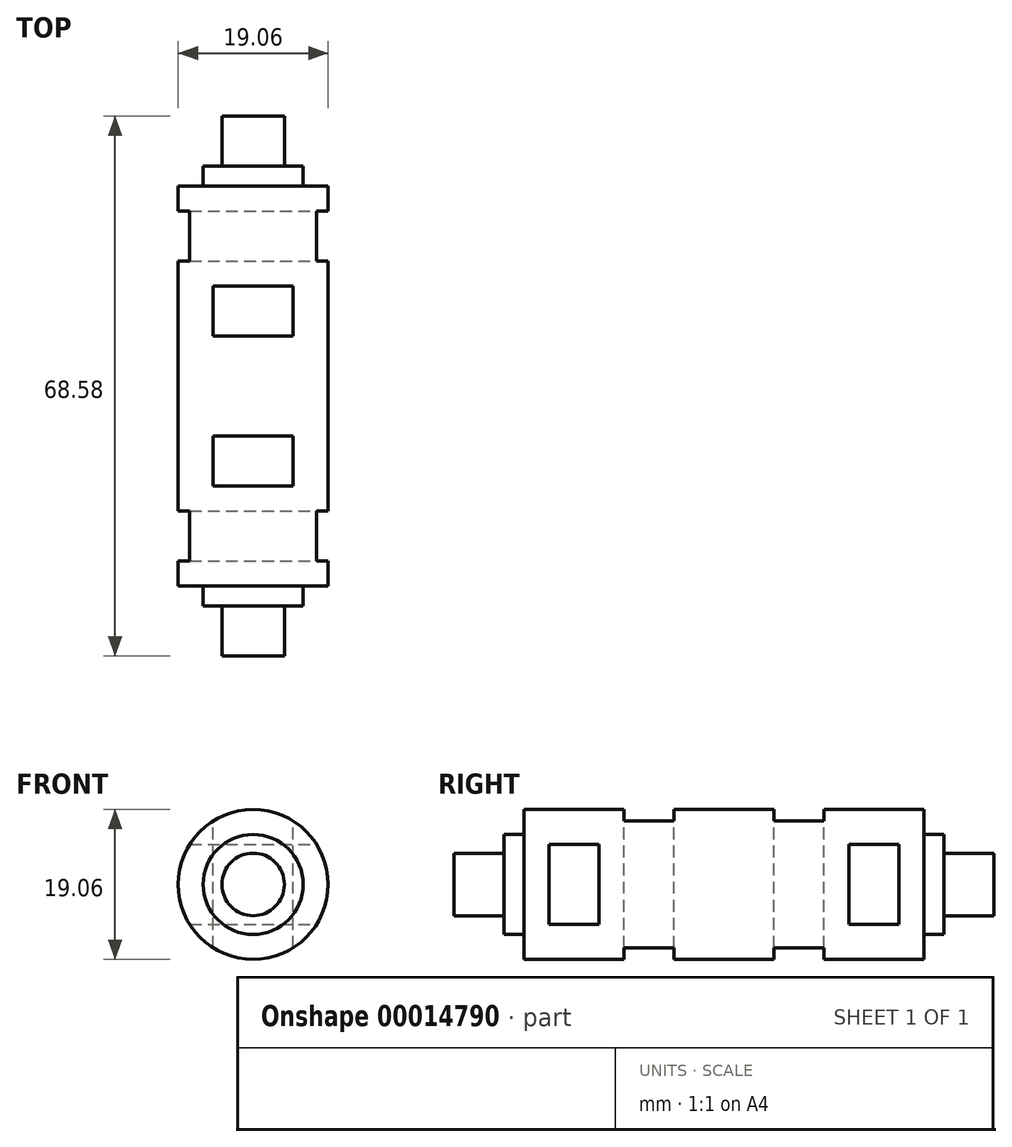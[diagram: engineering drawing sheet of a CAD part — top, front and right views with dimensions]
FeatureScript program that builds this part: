
annotation { "Feature Type Name" : "Feature", "Feature Type Description" : "" }
export const myFeature = defineFeature(function(context is Context, id is Id, definition is map)
    precondition{}
    {
        {
            var Q0;
            Q0=qCreatedBy(makeId("Front.planeOp"),FACE);
            var sketch = newSketch(context, id + "F0", { "sketchPlane" : qUnion([Q0])});
            skCircle(sketch, "E0", {"center": v(0, 0) * mm, "radius": 9.53 * mm});
            skSolve(sketch);
        }
        {
            var Q0;
            Q0=makeQuery(id+"F0.imprint","IMPRINT",FACE,{"disambiguationData":[TD([[makeQuery(id+"F0.imprint","IMPRINT",EDGE,{"derivedFrom":sQuery(id+"F0.wireOp",EDGE,"E0")}),1.0]])]});
            extrude(context, id + "F1", {"entities" : qUnion([Q0]), "depth" : 25.4 * mm, "hasSecondDirection" : true, "secondDirectionOppositeDirection" : true, "secondDirectionDepth" : 25.4 * mm});
        }
        {
            var Q0;
            Q0=makeQuery(id+"F1.opExtrude","CAP_FACE",FACE,{"disambiguationData":[OSD([sQuery(id+"F0.wireOp",EDGE,"E0")])],"isStart":false});
            var sketch = newSketch(context, id + "F2", { "sketchPlane" : qUnion([Q0])});
            skCircle(sketch, "E1", {"center": v(0, 0) * mm, "radius": 6.35 * mm});
            skSolve(sketch);
        }
        {
            var Q0;
            Q0=makeQuery(id+"F2.imprint","IMPRINT",FACE,{"disambiguationData":[TD([[makeQuery(id+"F2.imprint","IMPRINT",EDGE,{"derivedFrom":sQuery(id+"F2.wireOp",EDGE,"E1")}),1.0]])]});
            extrude(context, id + "F3", {"entities" : qUnion([Q0]), "operationType" : NewBodyOperationType.ADD, "depth" : 2.54 * mm});
        }
        {
            var Q0;
            Q0=makeQuery(id+"F3.opExtrude","CAP_FACE",FACE,{"disambiguationData":[OSD([sQuery(id+"F2.wireOp",EDGE,"E1")])],"isStart":false});
            var sketch = newSketch(context, id + "F4", { "sketchPlane" : qUnion([Q0])});
            skCircle(sketch, "E2", {"center": v(0, 0) * mm, "radius": 3.97 * mm});
            skSolve(sketch);
        }
        {
            var Q0;
            Q0=makeQuery(id+"F4.imprint","IMPRINT",FACE,{"disambiguationData":[TD([[makeQuery(id+"F4.imprint","IMPRINT",EDGE,{"derivedFrom":sQuery(id+"F4.wireOp",EDGE,"E2")}),1.0]])]});
            extrude(context, id + "F5", {"entities" : qUnion([Q0]), "operationType" : NewBodyOperationType.ADD, "depth" : 6.35 * mm});
        }
        {
            var Q0;
            Q0=makeQuery(id+"F1.opExtrude","CAP_FACE",FACE,{"disambiguationData":[OSD([sQuery(id+"F0.wireOp",EDGE,"E0")])],"isStart":true});
            var sketch = newSketch(context, id + "F6", { "sketchPlane" : qUnion([Q0])});
            skCircle(sketch, "E3", {"center": v(0, 0) * mm, "radius": 6.35 * mm});
            skSolve(sketch);
        }
        {
            var Q0;
            Q0=makeQuery(id+"F6.imprint","IMPRINT",FACE,{"disambiguationData":[TD([[makeQuery(id+"F6.imprint","IMPRINT",EDGE,{"derivedFrom":sQuery(id+"F6.wireOp",EDGE,"E3")}),1.0]])]});
            extrude(context, id + "F7", {"entities" : qUnion([Q0]), "operationType" : NewBodyOperationType.ADD, "depth" : 2.54 * mm});
        }
        {
            var Q0;
            Q0=makeQuery(id+"F7.opExtrude","CAP_FACE",FACE,{"disambiguationData":[OSD([sQuery(id+"F6.wireOp",EDGE,"E3")])],"isStart":false});
            var sketch = newSketch(context, id + "F8", { "sketchPlane" : qUnion([Q0])});
            skCircle(sketch, "E4", {"center": v(0, 0) * mm, "radius": 3.97 * mm});
            skSolve(sketch);
        }
        {
            var Q0;
            Q0 = qSketchRegion(id + "F8", true);
            extrude(context, id + "F9", {"entities" : qUnion([Q0]), "operationType" : NewBodyOperationType.ADD, "depth" : 6.35 * mm});
        }
        {
            var Q0;
            Q0=qCreatedBy(makeId("Top.planeOp"),FACE);
            var sketch = newSketch(context, id + "F10", { "sketchPlane" : qUnion([Q0])});
            skLineSegment(sketch, "E5.rect.bottom", {"start": v(5.08, 6.35) * mm, "end": v(-5.08, 6.35) * mm});
            skLineSegment(sketch, "E5.rect.top", {"start": v(5.08, 12.7) * mm, "end": v(-5.08, 12.7) * mm});
            skLineSegment(sketch, "E5.rect.left", {"start": v(5.08, 6.35) * mm, "end": v(5.08, 12.7) * mm});
            skLineSegment(sketch, "E5.rect.right", {"start": v(-5.08, 6.35) * mm, "end": v(-5.08, 12.7) * mm});
            skPoint(sketch, "E5.rect.middle", {"position": v(0, 9.53) * mm});
            skLineSegment(sketch, "E6.rect.bottom", {"start": v(5.08, -12.7) * mm, "end": v(-5.08, -12.7) * mm});
            skLineSegment(sketch, "E6.rect.top", {"start": v(5.08, -6.35) * mm, "end": v(-5.08, -6.35) * mm});
            skLineSegment(sketch, "E6.rect.left", {"start": v(5.08, -12.7) * mm, "end": v(5.08, -6.35) * mm});
            skLineSegment(sketch, "E6.rect.right", {"start": v(-5.08, -12.7) * mm, "end": v(-5.08, -6.35) * mm});
            skPoint(sketch, "E6.rect.middle", {"position": v(0, -9.52) * mm});
            skSolve(sketch);
        }
        {
            var Q0;
            Q0=qCreatedBy(makeId("Right.planeOp"),FACE);
            var sketch = newSketch(context, id + "F11", { "sketchPlane" : qUnion([Q0])});
            skLineSegment(sketch, "E7.rect.bottom", {"start": v(-15.88, -5.08) * mm, "end": v(-22.23, -5.08) * mm});
            skLineSegment(sketch, "E7.rect.top", {"start": v(-15.88, 5.08) * mm, "end": v(-22.22, 5.08) * mm});
            skLineSegment(sketch, "E7.rect.left", {"start": v(-15.88, -5.08) * mm, "end": v(-15.87, 5.08) * mm});
            skLineSegment(sketch, "E7.rect.right", {"start": v(-22.23, -5.08) * mm, "end": v(-22.22, 5.08) * mm});
            skPoint(sketch, "E7.rect.middle", {"position": v(-19.05, 0) * mm});
            skLineSegment(sketch, "E8.rect.bottom", {"start": v(22.22, -5.08) * mm, "end": v(15.88, -5.08) * mm});
            skLineSegment(sketch, "E8.rect.top", {"start": v(22.22, 5.08) * mm, "end": v(15.88, 5.08) * mm});
            skLineSegment(sketch, "E8.rect.left", {"start": v(22.22, -5.08) * mm, "end": v(22.22, 5.08) * mm});
            skLineSegment(sketch, "E8.rect.right", {"start": v(15.88, -5.08) * mm, "end": v(15.88, 5.08) * mm});
            skPoint(sketch, "E8.rect.middle", {"position": v(19.05, 0) * mm});
            skSolve(sketch);
        }
        {
            var Q0;
            Q0 = qSketchRegion(id + "F11", true);
            extrude(context, id + "F12", {"entities" : qUnion([Q0]), "operationType" : NewBodyOperationType.REMOVE, "oppositeDirection" : true, "depth" : 25.4 * mm, "hasSecondDirection" : true, "secondDirectionOppositeDirection" : false, "secondDirectionDepth" : 25.4 * mm});
        }
        {
            var Q0;
            Q0 = qSketchRegion(id + "F10", true);
            extrude(context, id + "F13", {"entities" : qUnion([Q0]), "operationType" : NewBodyOperationType.REMOVE, "oppositeDirection" : true, "depth" : 12.7 * mm, "hasSecondDirection" : true, "secondDirectionOppositeDirection" : false, "secondDirectionDepth" : 12.7 * mm});
        }
    });
